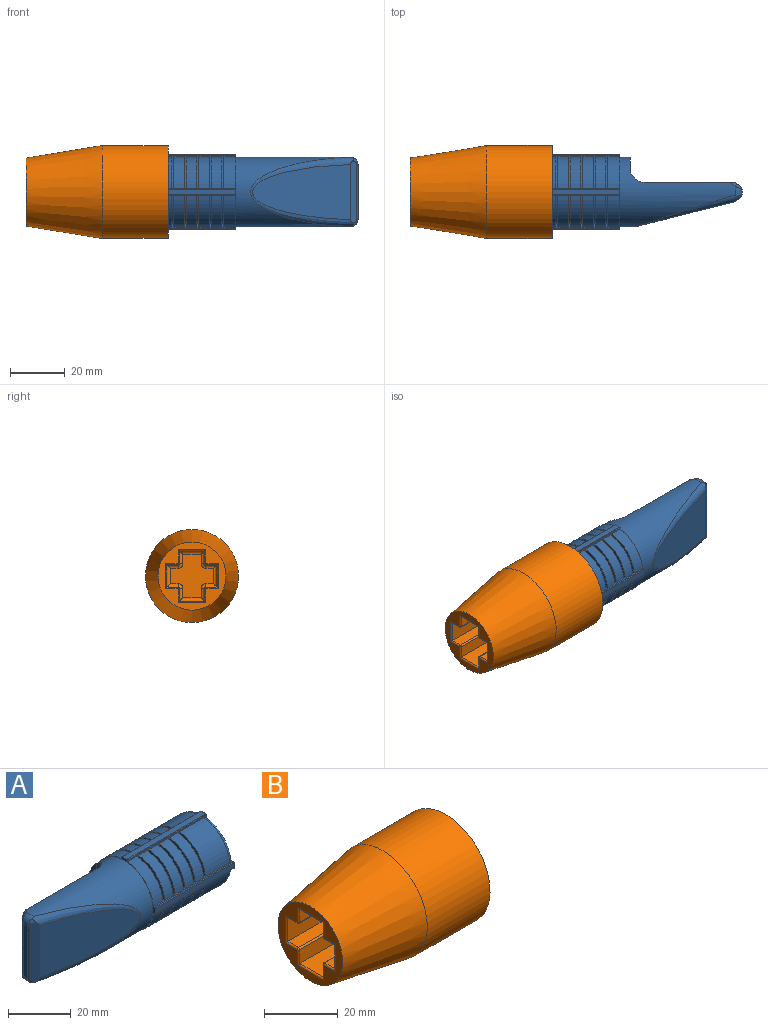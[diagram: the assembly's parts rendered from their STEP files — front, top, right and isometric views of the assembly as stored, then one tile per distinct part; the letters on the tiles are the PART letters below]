
ASSEMBLY  parts=2 mates=1
PART A: 136 faces, bbox 80.5x28.1x28.1 mm
  f0: cylinder r=12.95mm len=11.62mm, axis (-1,0,0), area 76.9mm2, adj f23,f87,f90,f97
  f1: cylinder r=12.95mm len=11.62mm, axis (-1,0,0), area 76.9mm2, adj f63,f90,f93,f98
  f2: cylinder r=12.95mm len=11.62mm, axis (-1,0,0), area 76.9mm2, adj f83,f90,f91,f96
  f3: cylinder r=12.95mm len=11.62mm, axis (-1,0,0), area 76.9mm2, adj f43,f89,f90,f94
  f4: cylinder r=12.95mm len=11.62mm, axis (-1,0,0), area 194.5mm2, adj f5,f87,f97,f135
  f5: plane 11.62x11.62mm, normal (-1,0,0), area 21.3mm2, adj f4,f6,f87,f97
  f6: cylinder r=11.68mm len=10.34mm, axis (-1,0,0), area 12mm2, adj f5,f7,f87,f97
  f7: plane 11.62x11.62mm, normal (1,0,0), area 21.3mm2, adj f6,f8,f87,f97
  f8: cylinder r=12.95mm len=11.62mm, axis (-1,0,0), area 67.8mm2, adj f7,f9,f87,f97
  f9: plane 11.62x11.62mm, normal (-1,0,0), area 21.3mm2, adj f8,f10,f87,f97
  f10: cylinder r=11.68mm len=10.34mm, axis (-1,0,0), area 12mm2, adj f9,f11,f87,f97
  f11: plane 11.62x11.62mm, normal (1,0,0), area 21.3mm2, adj f10,f12,f87,f97
  f12: cylinder r=12.95mm len=11.62mm, axis (-1,0,0), area 67.8mm2, adj f11,f13,f87,f97
  f13: plane 11.62x11.62mm, normal (-1,0,0), area 21.3mm2, adj f12,f14,f87,f97
  f14: cylinder r=11.68mm len=10.34mm, axis (-1,0,0), area 12mm2, adj f13,f15,f87,f97
  f15: plane 11.62x11.62mm, normal (1,0,0), area 21.3mm2, adj f14,f16,f87,f97
  f16: cylinder r=12.95mm len=11.62mm, axis (-1,0,0), area 67.8mm2, adj f15,f17,f87,f97
  f17: plane 11.62x11.62mm, normal (-1,0,0), area 21.3mm2, adj f16,f18,f87,f97
  f18: cylinder r=11.68mm len=10.34mm, axis (-1,0,0), area 12mm2, adj f17,f19,f87,f97
  f19: plane 11.62x11.62mm, normal (1,0,0), area 21.3mm2, adj f18,f20,f87,f97
  f20: cylinder r=12.95mm len=11.62mm, axis (-1,0,0), area 67.8mm2, adj f19,f21,f87,f97
  f21: plane 11.62x11.62mm, normal (-1,0,0), area 21.3mm2, adj f20,f22,f87,f97
  f22: cylinder r=11.68mm len=10.34mm, axis (-1,0,0), area 12mm2, adj f21,f23,f87,f97
  f23: plane 11.62x11.62mm, normal (1,0,0), area 21.3mm2, adj f0,f22,f87,f97
  f24: cylinder r=12.95mm len=11.62mm, axis (-1,0,0), area 194.5mm2, adj f25,f89,f94,f132
  f25: plane 11.62x11.62mm, normal (-1,0,0), area 21.3mm2, adj f24,f26,f89,f94
  f26: cylinder r=11.68mm len=10.34mm, axis (-1,0,0), area 12mm2, adj f25,f27,f89,f94
  f27: plane 11.62x11.62mm, normal (1,0,0), area 21.3mm2, adj f26,f28,f89,f94
  f28: cylinder r=12.95mm len=11.62mm, axis (-1,0,0), area 67.8mm2, adj f27,f29,f89,f94
  f29: plane 11.62x11.62mm, normal (-1,0,0), area 21.3mm2, adj f28,f30,f89,f94
  f30: cylinder r=11.68mm len=10.34mm, axis (-1,0,0), area 12mm2, adj f29,f31,f89,f94
  f31: plane 11.62x11.62mm, normal (1,0,0), area 21.3mm2, adj f30,f32,f89,f94
  f32: cylinder r=12.95mm len=11.62mm, axis (-1,0,0), area 67.8mm2, adj f31,f33,f89,f94
  f33: plane 11.62x11.62mm, normal (-1,0,0), area 21.3mm2, adj f32,f34,f89,f94
  f34: cylinder r=11.68mm len=10.34mm, axis (-1,0,0), area 12mm2, adj f33,f35,f89,f94
  f35: plane 11.62x11.62mm, normal (1,0,0), area 21.3mm2, adj f34,f36,f89,f94
  f36: cylinder r=12.95mm len=11.62mm, axis (-1,0,0), area 67.8mm2, adj f35,f37,f89,f94
  f37: plane 11.62x11.62mm, normal (-1,0,0), area 21.3mm2, adj f36,f38,f89,f94
  f38: cylinder r=11.68mm len=10.34mm, axis (-1,0,0), area 12mm2, adj f37,f39,f89,f94
  f39: plane 11.62x11.62mm, normal (1,0,0), area 21.3mm2, adj f38,f40,f89,f94
  f40: cylinder r=12.95mm len=11.62mm, axis (-1,0,0), area 67.8mm2, adj f39,f41,f89,f94
  f41: plane 11.62x11.62mm, normal (-1,0,0), area 21.3mm2, adj f40,f42,f89,f94
  f42: cylinder r=11.68mm len=10.34mm, axis (-1,0,0), area 12mm2, adj f41,f43,f89,f94
  f43: plane 11.62x11.62mm, normal (1,0,0), area 21.3mm2, adj f3,f42,f89,f94
  f44: cylinder r=12.95mm len=11.62mm, axis (-1,0,0), area 194.5mm2, adj f45,f93,f98,f131
  f45: plane 11.62x11.62mm, normal (-1,0,0), area 21.3mm2, adj f44,f46,f93,f98
  f46: cylinder r=11.68mm len=10.34mm, axis (-1,0,0), area 12mm2, adj f45,f47,f93,f98
  f47: plane 11.62x11.62mm, normal (1,0,0), area 21.3mm2, adj f46,f48,f93,f98
  f48: cylinder r=12.95mm len=11.62mm, axis (-1,0,0), area 67.8mm2, adj f47,f49,f93,f98
  f49: plane 11.62x11.62mm, normal (-1,0,0), area 21.3mm2, adj f48,f50,f93,f98
  f50: cylinder r=11.68mm len=10.34mm, axis (-1,0,0), area 12mm2, adj f49,f51,f93,f98
  f51: plane 11.62x11.62mm, normal (1,0,0), area 21.3mm2, adj f50,f52,f93,f98
  f52: cylinder r=12.95mm len=11.62mm, axis (-1,0,0), area 67.8mm2, adj f51,f53,f93,f98
  f53: plane 11.62x11.62mm, normal (-1,0,0), area 21.3mm2, adj f52,f54,f93,f98
  f54: cylinder r=11.68mm len=10.34mm, axis (-1,0,0), area 12mm2, adj f53,f55,f93,f98
  f55: plane 11.62x11.62mm, normal (1,0,0), area 21.3mm2, adj f54,f56,f93,f98
  f56: cylinder r=12.95mm len=11.62mm, axis (-1,0,0), area 67.8mm2, adj f55,f57,f93,f98
  f57: plane 11.62x11.62mm, normal (-1,0,0), area 21.3mm2, adj f56,f58,f93,f98
  f58: cylinder r=11.68mm len=10.34mm, axis (-1,0,0), area 12mm2, adj f57,f59,f93,f98
  f59: plane 11.62x11.62mm, normal (1,0,0), area 21.3mm2, adj f58,f60,f93,f98
  f60: cylinder r=12.95mm len=11.62mm, axis (-1,0,0), area 67.8mm2, adj f59,f61,f93,f98
  f61: plane 11.62x11.62mm, normal (-1,0,0), area 21.3mm2, adj f60,f62,f93,f98
  f62: cylinder r=11.68mm len=10.34mm, axis (-1,0,0), area 12mm2, adj f61,f63,f93,f98
  f63: plane 11.62x11.62mm, normal (1,0,0), area 21.3mm2, adj f1,f62,f93,f98
  f64: cylinder r=12.95mm len=11.62mm, axis (-1,0,0), area 194.5mm2, adj f65,f91,f96,f133
  f65: plane 11.62x11.62mm, normal (-1,0,0), area 21.3mm2, adj f64,f66,f91,f96
  f66: cylinder r=11.68mm len=10.34mm, axis (-1,0,0), area 12mm2, adj f65,f67,f91,f96
  f67: plane 11.62x11.62mm, normal (1,0,0), area 21.3mm2, adj f66,f68,f91,f96
  f68: cylinder r=12.95mm len=11.62mm, axis (-1,0,0), area 67.8mm2, adj f67,f69,f91,f96
  f69: plane 11.62x11.62mm, normal (-1,0,0), area 21.3mm2, adj f68,f70,f91,f96
  f70: cylinder r=11.68mm len=10.34mm, axis (-1,0,0), area 12mm2, adj f69,f71,f91,f96
  f71: plane 11.62x11.62mm, normal (1,0,0), area 21.3mm2, adj f70,f72,f91,f96
  f72: cylinder r=12.95mm len=11.62mm, axis (-1,0,0), area 67.8mm2, adj f71,f73,f91,f96
  f73: plane 11.62x11.62mm, normal (-1,0,0), area 21.3mm2, adj f72,f74,f91,f96
  f74: cylinder r=11.68mm len=10.34mm, axis (-1,0,0), area 12mm2, adj f73,f75,f91,f96
  f75: plane 11.62x11.62mm, normal (1,0,0), area 21.3mm2, adj f74,f76,f91,f96
  f76: cylinder r=12.95mm len=11.62mm, axis (-1,0,0), area 67.8mm2, adj f75,f77,f91,f96
  f77: plane 11.62x11.62mm, normal (-1,0,0), area 21.3mm2, adj f76,f78,f91,f96
  f78: cylinder r=11.68mm len=10.34mm, axis (-1,0,0), area 12mm2, adj f77,f79,f91,f96
  f79: plane 11.62x11.62mm, normal (1,0,0), area 21.3mm2, adj f78,f80,f91,f96
  f80: cylinder r=12.95mm len=11.62mm, axis (-1,0,0), area 67.8mm2, adj f79,f81,f91,f96
  f81: plane 11.62x11.62mm, normal (-1,0,0), area 21.3mm2, adj f80,f82,f91,f96
  f82: cylinder r=11.68mm len=10.34mm, axis (-1,0,0), area 12mm2, adj f81,f83,f91,f96
  f83: plane 11.62x11.62mm, normal (1,0,0), area 21.3mm2, adj f2,f82,f91,f96
  f84: plane 18.8x18.8mm, normal (1,0,0), area 277.5mm2, adj f85
  f85: cylinder r=9.4mm len=34.29mm, axis (-1,0,0), area 2024.8mm2, adj f84,f134
  f86: plane 26.92x26.92mm, normal (1,0,0), area 89.6mm2, adj f87,f89,f91,f93,f94,f96,f97,f98
  f87: plane 35.62x1.91mm, normal (0,-1,0), area 25.5mm2, adj f0,f4,f5,f6,f7,f8,f9,f10
  f88: plane 35.31x2.03mm, normal (0,0,-1), area 71.7mm2, adj f90,f114,f115,f116
  f89: plane 35.62x1.91mm, normal (0,1,0), area 25.5mm2, adj f3,f24,f25,f26,f27,f28,f29,f30
  f90: plane 27.43x27.43mm, normal (-1,0,0), area 28.3mm2, adj f0,f1,f2,f3,f87,f88,f89,f91
  f91: plane 35.62x1.91mm, normal (0,1,0), area 25.5mm2, adj f2,f64,f65,f66,f67,f68,f69,f70
  f92: plane 35.31x2.03mm, normal (0,0,1), area 71.7mm2, adj f90,f120,f121,f122
  f93: plane 35.62x1.91mm, normal (0,-1,0), area 25.5mm2, adj f1,f44,f45,f46,f47,f48,f49,f50
  f94: plane 35.62x1.91mm, normal (0,0,-1), area 25.5mm2, adj f3,f24,f25,f26,f27,f28,f29,f30
  f95: plane 35.31x2.03mm, normal (0,1,0), area 71.7mm2, adj f90,f117,f118,f119
  f96: plane 35.62x1.91mm, normal (0,0,1), area 25.5mm2, adj f2,f64,f65,f66,f67,f68,f69,f70
  f97: plane 35.62x1.91mm, normal (0,0,-1), area 25.5mm2, adj f0,f4,f5,f6,f7,f8,f9,f10
  f98: plane 35.62x1.91mm, normal (0,0,1), area 25.5mm2, adj f1,f44,f45,f46,f47,f48,f49,f50
  f99: plane 35.31x2.03mm, normal (0,-1,0), area 71.7mm2, adj f90,f111,f112,f113
  f100: cylinder r=12.7mm len=42.16mm, axis (1,0,0), area 1234.5mm2, adj f90,f101,f106,f107,f108,f109,f110,f123
  f101: plane 33.02x24.38mm, normal (0,1,0), area 804.4mm2, adj f100,f102,f107,f123,f127
  f102: plane 22.59x2.26mm, normal (-0.58,0.82,0), area 61.7mm2, adj f101,f123,f124,f125,f126,f127
  f103: plane 20.32x1.84mm, normal (-1,0,0), area 37.3mm2, adj f108,f110,f125,f129
  f104: plane 22.82x2.49mm, normal (-0.58,-0.82,0), area 61.2mm2, adj f105,f109,f128,f129,f130
  f105: plane 35.79x20.2mm, normal (-0.25,-0.97,0), area 569.9mm2, adj f104,f109
  f106: plane 18.62x4.06mm, normal (-1,0,0), area 52.3mm2, adj f100,f107
  f107: cylinder r=5.08mm len=24.38mm, axis (0,0,1), area 171.6mm2, adj f100,f101,f106
  f108: torus R=10.16mm, axis (1,0,0), area 10.4mm2, adj f100,f103,f109,f124,f128
  f109: bspline ~37.96x25.34mm, area 198mm2, adj f100,f104,f105,f108,f110,f128,f130
  f110: torus R=10.16mm, axis (1,0,0), area 10.4mm2, adj f100,f103,f109,f126,f130
  f111: cylinder r=0.25mm len=35.56mm, axis (-1,0,0), area 14.1mm2, adj f90,f98,f99,f112
  f112: cylinder r=0.25mm len=2.54mm, axis (0,0,1), area 0.9mm2, adj f86,f99,f111,f113
  f113: cylinder r=0.25mm len=35.56mm, axis (1,0,0), area 14.1mm2, adj f90,f97,f99,f112
  f114: cylinder r=0.25mm len=35.56mm, axis (-1,0,0), area 14.1mm2, adj f88,f89,f90,f115
  f115: cylinder r=0.25mm len=2.54mm, axis (0,-1,0), area 0.9mm2, adj f86,f88,f114,f116
  f116: cylinder r=0.25mm len=35.56mm, axis (1,0,0), area 14.1mm2, adj f87,f88,f90,f115
  f117: cylinder r=0.25mm len=35.56mm, axis (1,0,0), area 14.1mm2, adj f90,f95,f96,f118
  f118: cylinder r=0.25mm len=2.54mm, axis (0,0,-1), area 0.9mm2, adj f86,f95,f117,f119
  f119: cylinder r=0.25mm len=35.56mm, axis (-1,0,0), area 14.1mm2, adj f90,f94,f95,f118
  f120: cylinder r=0.25mm len=35.56mm, axis (1,0,0), area 14.1mm2, adj f90,f91,f92,f121
  f121: cylinder r=0.25mm len=2.54mm, axis (0,1,0), area 0.9mm2, adj f86,f92,f120,f122
  f122: cylinder r=0.25mm len=35.56mm, axis (-1,0,0), area 14.1mm2, adj f90,f92,f93,f121
  f123: bspline ~2.68x2.22mm, area 3mm2, adj f100,f101,f102,f124
  f124: bspline ~3.23x2.95mm, area 4.6mm2, adj f102,f108,f123,f125
  f125: cylinder r=1.27mm len=20.24mm, axis (0,0,1), area 24.5mm2, adj f102,f103,f124,f126
  f126: bspline ~3.23x2.94mm, area 4.6mm2, adj f102,f110,f125,f127
  f127: bspline ~2.68x2.22mm, area 3mm2, adj f100,f101,f102,f126
  f128: bspline ~4.14x3.07mm, area 3.9mm2, adj f104,f108,f109,f129
  f129: cylinder r=1.27mm len=20.24mm, axis (0,0,-1), area 24.5mm2, adj f103,f104,f128,f130
  f130: bspline ~4.14x3.07mm, area 3.9mm2, adj f104,f109,f110,f129
  f131: torus R=11.68mm, axis (-1,0,0), area 34mm2, adj f44,f86,f93,f98
  f132: torus R=11.68mm, axis (-1,0,0), area 34mm2, adj f24,f86,f89,f94
  f133: torus R=11.68mm, axis (-1,0,0), area 34mm2, adj f64,f86,f91,f96
  f134: torus R=10.67mm, axis (-1,0,0), area 123.6mm2, adj f85,f86
  f135: torus R=11.68mm, axis (-1,0,0), area 34mm2, adj f4,f86,f87,f97
PART B: 108 faces, bbox 52.1x34x34 mm
  f0: cylinder r=13.21mm len=31.24mm, axis (-1,0,0), area 525.5mm2, adj f10,f51,f56,f57
  f1: cylinder r=13.21mm len=31.24mm, axis (-1,0,0), area 525.5mm2, adj f10,f48,f54,f55
  f2: cylinder r=13.21mm len=31.24mm, axis (-1,0,0), area 525.5mm2, adj f10,f64,f67,f70
  f3: plane 34.04x34.04mm, normal (1,0,0), area 305.6mm2, adj f12,f40,f44,f45,f46,f47,f49,f50
  f4: plane 24.89x24.89mm, normal (-1,0,0), area 206.9mm2, adj f38,f74,f75,f76,f77,f79,f80,f84
  f5: plane 13.4x13.4mm, normal (1,0,0), area 140.9mm2, adj f6
  f6: torus R=6.7mm, axis (-1,0,0), area 34.4mm2, adj f5,f7
  f7: cone r=7.37mm half-angle=2deg, axis (-1,0,0), area 210.2mm2, adj f6,f8
  f8: plane 17.27x17.27mm, normal (1,0,0), area 63.8mm2, adj f7,f71
  f9: cylinder r=9.14mm len=24.13mm, axis (-1,0,0), area 1386.4mm2, adj f10,f71
  f10: plane 27.94x27.94mm, normal (1,0,0), area 295.3mm2, adj f0,f1,f2,f9,f11,f26,f27,f28
  f11: cylinder r=13.21mm len=31.24mm, axis (-1,0,0), area 525.5mm2, adj f10,f39,f40,f41
  f12: cylinder r=17.02mm len=34.04mm, axis (-1,0,0), area 2580.2mm2, adj f3,f38
  f13: plane 13.46x4.57mm, normal (0,1,0), area 61.5mm2, adj f14,f81,f85,f92
  f14: plane 13.46x9.14mm, normal (0,0,-1), area 123.1mm2, adj f13,f15,f87,f93
  f15: plane 13.46x4.57mm, normal (0,-1,0), area 61.5mm2, adj f14,f89,f91,f95
  f16: plane 13.46x4.06mm, normal (0,0,-1), area 54.7mm2, adj f17,f88,f91,f99
  f17: plane 13.46x8.13mm, normal (0,-1,0), area 109.4mm2, adj f16,f18,f86,f101
  f18: plane 13.46x4.06mm, normal (0,0,1), area 54.7mm2, adj f17,f78,f84,f103
  f19: plane 13.46x4.57mm, normal (0,-1,0), area 61.5mm2, adj f20,f78,f79,f107
  f20: plane 13.46x9.14mm, normal (0,0,1), area 123.1mm2, adj f19,f21,f76,f106
  f21: plane 13.46x4.57mm, normal (0,1,0), area 61.5mm2, adj f20,f72,f74,f104
  f22: plane 13.46x4.06mm, normal (0,0,1), area 54.7mm2, adj f23,f72,f75,f100
  f23: plane 13.46x8.13mm, normal (0,1,0), area 109.4mm2, adj f22,f24,f77,f98
  f24: plane 13.46x4.06mm, normal (0,0,-1), area 54.7mm2, adj f23,f80,f81,f96
  f25: plane 15.75x15.75mm, normal (-1,0,0), area 157.8mm2, adj f92,f93,f94,f95,f96,f97,f98,f99
  f26: plane 31.24x0.41mm, normal (0,0,1), area 12.7mm2, adj f10,f27,f41,f45
  f27: plane 31.24x3.05mm, normal (0,-1,0), area 95.2mm2, adj f10,f26,f28,f47
  f28: plane 31.24x0.41mm, normal (0,0,-1), area 12.7mm2, adj f10,f27,f50,f51
  f29: plane 31.24x0.41mm, normal (0,0,1), area 12.7mm2, adj f10,f31,f54,f60
  f30: plane 31.24x0.41mm, normal (0,0,-1), area 12.7mm2, adj f10,f31,f64,f65
  f31: plane 31.24x3.05mm, normal (0,1,0), area 95.2mm2, adj f10,f29,f30,f62
  f32: plane 31.24x0.41mm, normal (0,-1,0), area 12.7mm2, adj f10,f34,f39,f44
  f33: plane 31.24x0.41mm, normal (0,1,0), area 12.7mm2, adj f10,f34,f48,f49
  f34: plane 31.24x3.05mm, normal (0,0,1), area 95.2mm2, adj f10,f32,f33,f46
  f35: plane 31.24x0.41mm, normal (0,-1,0), area 12.7mm2, adj f10,f36,f57,f61
  f36: plane 31.24x3.05mm, normal (0,0,-1), area 95.2mm2, adj f10,f35,f37,f63
  f37: plane 31.24x0.41mm, normal (0,1,0), area 12.7mm2, adj f10,f36,f66,f67
  f38: cone r=12.45mm half-angle=9.3deg, axis (1,0,0), area 2620.6mm2, adj f4,f12
  f39: cylinder r=0.51mm len=31.24mm, axis (-1,0,0), area 22.6mm2, adj f10,f11,f32,f42
  f40: torus R=13.72mm, axis (-1,0,0), area 13.6mm2, adj f3,f11,f42,f43
  f41: cylinder r=0.51mm len=31.24mm, axis (-1,0,0), area 22.6mm2, adj f10,f11,f26,f43
  f42: sphere r=0.51mm, area 0.4mm2, adj f39,f40,f44
  f43: sphere r=0.51mm, area 0.4mm2, adj f40,f41,f45
  f44: cylinder r=0.51mm len=0.91mm, axis (0,0,1), area 0.5mm2, adj f3,f32,f42,f46
  f45: cylinder r=0.51mm len=0.91mm, axis (0,1,0), area 0.5mm2, adj f3,f26,f43,f47
  f46: cylinder r=0.51mm len=4.06mm, axis (0,1,0), area 2.7mm2, adj f3,f34,f44,f49
  f47: cylinder r=0.51mm len=4.06mm, axis (0,0,1), area 2.7mm2, adj f3,f27,f45,f50
  f48: cylinder r=0.51mm len=31.24mm, axis (-1,0,0), area 22.6mm2, adj f1,f10,f33,f52
  f49: cylinder r=0.51mm len=0.91mm, axis (0,0,-1), area 0.5mm2, adj f3,f33,f46,f52
  f50: cylinder r=0.51mm len=0.91mm, axis (0,-1,0), area 0.5mm2, adj f3,f28,f47,f53
  f51: cylinder r=0.51mm len=31.24mm, axis (-1,0,0), area 22.6mm2, adj f0,f10,f28,f53
  f52: sphere r=0.51mm, area 0.4mm2, adj f48,f49,f55
  f53: sphere r=0.51mm, area 0.4mm2, adj f50,f51,f56
  f54: cylinder r=0.51mm len=31.24mm, axis (-1,0,0), area 22.6mm2, adj f1,f10,f29,f58
  f55: torus R=13.72mm, axis (-1,0,0), area 13.6mm2, adj f1,f3,f52,f58
  f56: torus R=13.72mm, axis (-1,0,0), area 13.6mm2, adj f0,f3,f53,f59
  f57: cylinder r=0.51mm len=31.24mm, axis (-1,0,0), area 22.6mm2, adj f0,f10,f35,f59
  f58: sphere r=0.51mm, area 0.4mm2, adj f54,f55,f60
  f59: sphere r=0.51mm, area 0.4mm2, adj f56,f57,f61
  f60: cylinder r=0.51mm len=0.91mm, axis (0,1,0), area 0.5mm2, adj f3,f29,f58,f62
  f61: cylinder r=0.51mm len=0.91mm, axis (0,0,1), area 0.5mm2, adj f3,f35,f59,f63
  f62: cylinder r=0.51mm len=4.06mm, axis (0,0,-1), area 2.7mm2, adj f3,f31,f60,f65
  f63: cylinder r=0.51mm len=4.06mm, axis (0,-1,0), area 2.7mm2, adj f3,f36,f61,f66
  f64: cylinder r=0.51mm len=31.24mm, axis (-1,0,0), area 22.6mm2, adj f2,f10,f30,f68
  f65: cylinder r=0.51mm len=0.91mm, axis (0,-1,0), area 0.5mm2, adj f3,f30,f62,f68
  f66: cylinder r=0.51mm len=0.91mm, axis (0,0,-1), area 0.5mm2, adj f3,f37,f63,f69
  f67: cylinder r=0.51mm len=31.24mm, axis (-1,0,0), area 22.6mm2, adj f2,f10,f37,f69
  f68: sphere r=0.51mm, area 0.4mm2, adj f64,f65,f70
  f69: sphere r=0.51mm, area 0.4mm2, adj f66,f67,f70
  f70: torus R=13.72mm, axis (-1,0,0), area 13.6mm2, adj f2,f3,f68,f69
  f71: torus R=8.64mm, axis (1,0,0), area 44.9mm2, adj f8,f9
  f72: cylinder r=0.51mm len=13.46mm, axis (-1,0,0), area 10.7mm2, adj f21,f22,f73,f102
  f73: sphere r=0.51mm, area 0.4mm2, adj f72,f74,f75
  f74: cylinder r=0.51mm len=5.08mm, axis (0,0,-1), area 3.8mm2, adj f4,f21,f73,f76
  f75: cylinder r=0.51mm len=4.57mm, axis (0,1,0), area 3.4mm2, adj f4,f22,f73,f77
  f76: cylinder r=0.51mm len=10.16mm, axis (0,1,0), area 7.6mm2, adj f4,f20,f74,f79
  f77: cylinder r=0.51mm len=9.14mm, axis (0,0,-1), area 6.8mm2, adj f4,f23,f75,f80
  f78: cylinder r=0.51mm len=13.46mm, axis (1,0,0), area 10.7mm2, adj f18,f19,f82,f105
  f79: cylinder r=0.51mm len=5.08mm, axis (0,0,1), area 3.8mm2, adj f4,f19,f76,f82
  f80: cylinder r=0.51mm len=4.57mm, axis (0,-1,0), area 3.4mm2, adj f4,f24,f77,f83
  f81: cylinder r=0.51mm len=13.46mm, axis (1,0,0), area 10.7mm2, adj f13,f24,f83,f94
  f82: sphere r=0.51mm, area 0.4mm2, adj f78,f79,f84
  f83: sphere r=0.51mm, area 0.4mm2, adj f80,f81,f85
  f84: cylinder r=0.51mm len=4.57mm, axis (0,1,0), area 3.4mm2, adj f4,f18,f82,f86
  f85: cylinder r=0.51mm len=5.08mm, axis (0,0,-1), area 3.8mm2, adj f4,f13,f83,f87
  f86: cylinder r=0.51mm len=9.14mm, axis (0,0,1), area 6.8mm2, adj f4,f17,f84,f88
  f87: cylinder r=0.51mm len=10.16mm, axis (0,-1,0), area 7.6mm2, adj f4,f14,f85,f89
  f88: cylinder r=0.51mm len=4.57mm, axis (0,-1,0), area 3.4mm2, adj f4,f16,f86,f90
  f89: cylinder r=0.51mm len=5.08mm, axis (0,0,1), area 3.8mm2, adj f4,f15,f87,f90
  f90: sphere r=0.51mm, area 0.4mm2, adj f88,f89,f91
  f91: cylinder r=0.51mm len=13.46mm, axis (-1,0,0), area 10.7mm2, adj f15,f16,f90,f97
  f92: cylinder r=1.27mm len=4.57mm, axis (0,0,1), area 8.2mm2, adj f13,f25,f93,f94
  f93: cylinder r=1.27mm len=9.14mm, axis (0,1,0), area 16.4mm2, adj f14,f25,f92,f95
  f94: torus R=1.78mm, axis (-1,0,0), area 3mm2, adj f25,f81,f92,f96
  f95: cylinder r=1.27mm len=4.57mm, axis (0,0,-1), area 8.2mm2, adj f15,f25,f93,f97
  f96: cylinder r=1.27mm len=4.06mm, axis (0,1,0), area 7.2mm2, adj f24,f25,f94,f98
  f97: torus R=1.78mm, axis (-1,0,0), area 3mm2, adj f25,f91,f95,f99
  f98: cylinder r=1.27mm len=8.13mm, axis (0,0,1), area 14.4mm2, adj f23,f25,f96,f100
  f99: cylinder r=1.27mm len=4.06mm, axis (0,1,0), area 7.2mm2, adj f16,f25,f97,f101
  f100: cylinder r=1.27mm len=4.06mm, axis (0,-1,0), area 7.2mm2, adj f22,f25,f98,f102
  f101: cylinder r=1.27mm len=8.13mm, axis (0,0,-1), area 14.4mm2, adj f17,f25,f99,f103
  f102: torus R=1.78mm, axis (-1,0,0), area 3mm2, adj f25,f72,f100,f104
  f103: cylinder r=1.27mm len=4.06mm, axis (0,-1,0), area 7.2mm2, adj f18,f25,f101,f105
  f104: cylinder r=1.27mm len=4.57mm, axis (0,0,1), area 8.2mm2, adj f21,f25,f102,f106
  f105: torus R=1.78mm, axis (-1,0,0), area 3mm2, adj f25,f78,f103,f107
  f106: cylinder r=1.27mm len=9.14mm, axis (0,-1,0), area 16.4mm2, adj f20,f25,f104,f107
  f107: cylinder r=1.27mm len=4.57mm, axis (0,0,-1), area 8.2mm2, adj f19,f25,f105,f106
PLACE A rot(axis=(0,1,0),180deg) t=(-16.74,-67.51,-17.03)mm
PLACE B t=(-97.27,-67.51,-17.03)mm fixed
MATE slider A.f0 <-> B.f0  axis (1,0,0) through (-20.55,-67.51,-17.03)mm
